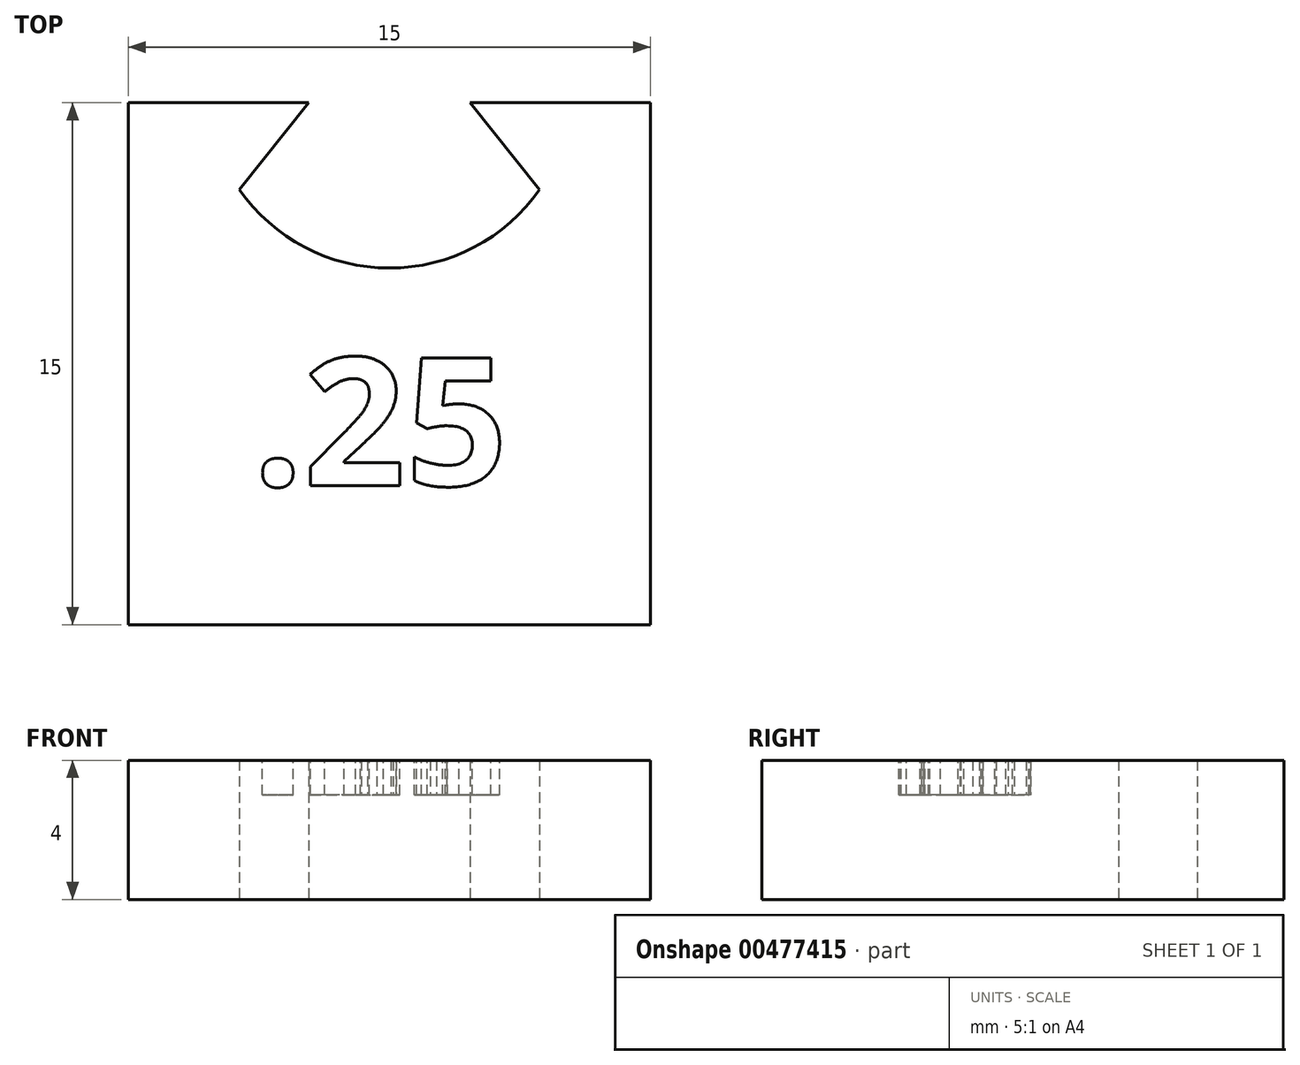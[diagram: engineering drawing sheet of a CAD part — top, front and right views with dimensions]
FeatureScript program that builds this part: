
annotation { "Feature Type Name" : "Feature", "Feature Type Description" : "" }
export const myFeature = defineFeature(function(context is Context, id is Id, definition is map)
    precondition{}
    {
        {
            var Q0;
            Q0=qCreatedBy(makeId("Top.planeOp"),FACE);
            var sketch = newSketch(context, id + "F0", { "sketchPlane" : qUnion([Q0])});
            skLineSegment(sketch, "E0.bottom", {"start": v(7.5, 7.5) * mm, "end": v(-7.5, 7.5) * mm});
            skLineSegment(sketch, "E0.top", {"start": v(7.5, -7.5) * mm, "end": v(-7.5, -7.5) * mm});
            skLineSegment(sketch, "E0.left", {"start": v(7.5, 7.5) * mm, "end": v(7.5, -7.5) * mm});
            skLineSegment(sketch, "E0.right", {"start": v(-7.5, 7.5) * mm, "end": v(-7.5, -7.5) * mm});
            skPoint(sketch, "E0.middle", {"position": v(0, 0) * mm});
            skLineSegment(sketch, "E1", {"start": v(0, 0) * mm, "end": v(0, 12.76) * mm});
            skLineSegment(sketch, "E2", {"start": v(-2, 7.5) * mm, "end": v(-4, 5) * mm});
            skLineSegment(sketch, "E3", {"start": v(2, 7.5) * mm, "end": v(4, 5) * mm});
            skArc(sketch, "E4", {"start": v(-4, 5) * mm, "mid": v(0, 3) * mm, "end": v(4, 5) * mm});
            skLineSegment(sketch, "E5.0", {"start": v(2.2, 7.66) * mm, "end": v(4.31, 5) * mm});
            skArc(sketch, "E5.1", {"start": v(-4.31, 5) * mm, "mid": v(0, 2.75) * mm, "end": v(4.31, 5) * mm});
            skLineSegment(sketch, "E5.2", {"start": v(-2.2, 7.66) * mm, "end": v(-4.31, 5) * mm});
            skSolve(sketch);
        }
        {
            var Q0;
            Q0=makeQuery(id+"F0.imprint","IMPRINT",FACE,{"disambiguationData":[TD([[makeQuery(id+"F0.imprint","IMPRINT",EDGE,{"derivedFrom":sQuery(id+"F0.wireOp",EDGE,"E0.top")}),-1.0]])]});
            extrude(context, id + "F1", {"entities" : qUnion([Q0]), "depth" : 4 * mm, "offsetDistance" : 25 * mm});
        }
        {
            var Q0;
            Q0=makeQuery(id+"F1.opExtrude","CAP_FACE",FACE,{"disambiguationData":[OSD([sQuery(id+"F0.wireOp",EDGE,"E0.bottom"),sQuery(id+"F0.wireOp",EDGE,"E0.top"),sQuery(id+"F0.wireOp",EDGE,"E0.left"),sQuery(id+"F0.wireOp",EDGE,"E0.right"),sQuery(id+"F0.wireOp",EDGE,"E5.0"),sQuery(id+"F0.wireOp",EDGE,"E5.1"),sQuery(id+"F0.wireOp",EDGE,"E5.2")])],"isStart":false});
            var sketch = newSketch(context, id + "F2", { "sketchPlane" : qUnion([Q0])});
            skText(sketch, "E6", { "text": ".25\n\n\n\n", "fontName": "OpenSans-Bold.ttf"});
            const initialGuessF2  = {"E6": [-0.00394, -0.0035, 1, 0, 0.0037]};
            skSetInitialGuess(sketch, initialGuessF2);
            skSolve(sketch);
        }
        {
            var Q0;
            Q0 = qSketchRegion(id + "F2", true);
            extrude(context, id + "F3", {"entities" : qUnion([Q0]), "operationType" : NewBodyOperationType.REMOVE, "oppositeDirection" : true, "depth" : 1 * mm, "offsetDistance" : 25 * mm});
        }
    });
